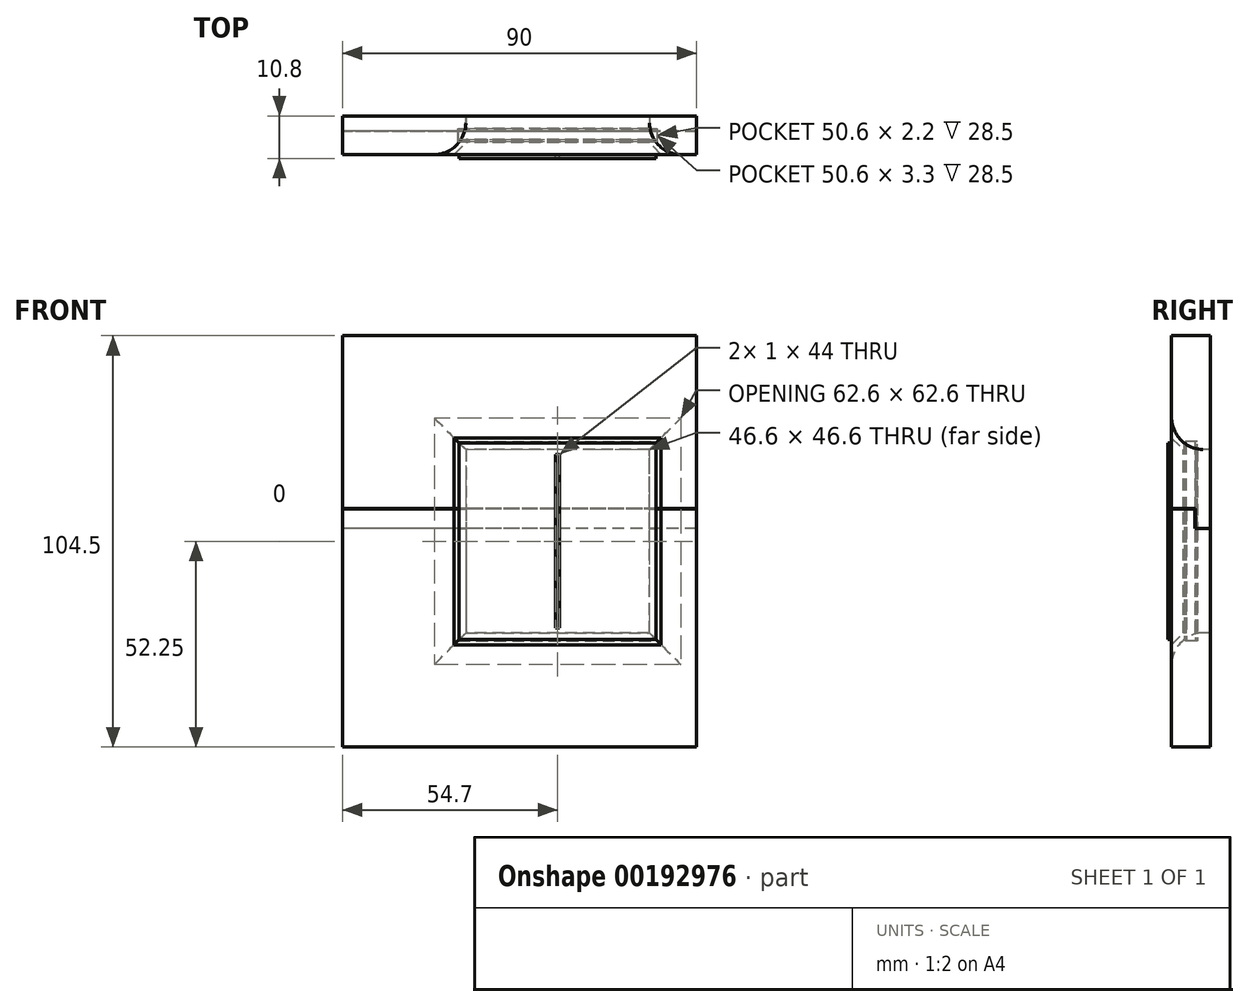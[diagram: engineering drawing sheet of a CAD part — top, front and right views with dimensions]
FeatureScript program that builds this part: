
annotation { "Feature Type Name" : "Feature", "Feature Type Description" : "" }
export const myFeature = defineFeature(function(context is Context, id is Id, definition is map)
    precondition{}
    {
        {
            var Q0;
            Q0=qCreatedBy(makeId("Front.planeOp"),FACE);
            var sketch = newSketch(context, id + "F0", { "sketchPlane" : qUnion([Q0])});
            skLineSegment(sketch, "E0", {"start": v(45, 5) * mm, "end": v(45, 109.5) * mm});
            skLineSegment(sketch, "E1", {"start": v(45, 109.5) * mm, "end": v(-45, 109.5) * mm});
            skLineSegment(sketch, "E2", {"start": v(-45, 109.5) * mm, "end": v(-45, 5) * mm});
            skLineSegment(sketch, "E3", {"start": v(45, 5) * mm, "end": v(-45, 5) * mm});
            skLineSegment(sketch, "E4", {"start": v(-15.6, 31.95) * mm, "end": v(35, 31.95) * mm});
            skLineSegment(sketch, "E5", {"start": v(35, 31.95) * mm, "end": v(35, 82.55) * mm});
            skLineSegment(sketch, "E6", {"start": v(-15.6, 82.55) * mm, "end": v(-15.6, 31.95) * mm});
            skLineSegment(sketch, "E7", {"start": v(-13.6, 80.55) * mm, "end": v(-13.6, 33.95) * mm});
            skLineSegment(sketch, "E8", {"start": v(33, 33.95) * mm, "end": v(33, 80.55) * mm});
            skLineSegment(sketch, "E9", {"start": v(45, 80.55) * mm, "end": v(-45, 80.55) * mm});
            skLineSegment(sketch, "E10", {"start": v(0, 0) * mm, "end": v(0, 125.52) * mm, "construction": true});
            skPoint(sketch, "E11", {"position": v(45, 57.25) * mm});
            skLineSegment(sketch, "E12", {"start": v(78.43, 57.25) * mm, "end": v(-79.16, 57.25) * mm, "construction": true});
            skPoint(sketch, "E13.orphan", {"position": v(-45, 57.25) * mm});
            skPoint(sketch, "E14", {"position": v(-15.6, 80.55) * mm});
            skPoint(sketch, "E15", {"position": v(35, 80.55) * mm});
            skPoint(sketch, "E16", {"position": v(0, 109.5) * mm});
            skPoint(sketch, "E17", {"position": v(0, 5) * mm});
            skPoint(sketch, "E18", {"position": v(35, 57.25) * mm});
            skPoint(sketch, "E19", {"position": v(33, 57.25) * mm});
            skPoint(sketch, "E20", {"position": v(-13.6, 57.25) * mm});
            skPoint(sketch, "E21", {"position": v(-15.6, 57.25) * mm});
            skPoint(sketch, "E22", {"position": v(0, 57.25) * mm});
            skLineSegment(sketch, "E23", {"start": v(33, 33.95) * mm, "end": v(-13.6, 33.95) * mm});
            skLineSegment(sketch, "E24", {"start": v(9.7, 159.6) * mm, "end": v(9.7, -24.97) * mm, "construction": true});
            skPoint(sketch, "E25", {"position": v(9.7, 5) * mm});
            skPoint(sketch, "E26", {"position": v(9.7, 31.95) * mm});
            skPoint(sketch, "E27", {"position": v(9.7, 33.95) * mm});
            skPoint(sketch, "E28", {"position": v(-45, 82.55) * mm});
            skLineSegment(sketch, "E29", {"start": v(-45, 82.55) * mm, "end": v(45, 82.55) * mm});
            skSolve(sketch);
        }
        {
            var Q0;
            Q0=qCreatedBy(makeId("Top.planeOp"),FACE);
            var sketch = newSketch(context, id + "F1", { "sketchPlane" : qUnion([Q0])});
            skLineSegment(sketch, "E30", {"start": v(-44.9, 9.8) * mm, "end": v(44.9, 9.8) * mm});
            skLineSegment(sketch, "E31", {"start": v(44.9, 9.8) * mm, "end": v(44.9, 0) * mm});
            skLineSegment(sketch, "E32", {"start": v(44.9, 0) * mm, "end": v(-44.9, 0) * mm});
            skLineSegment(sketch, "E33", {"start": v(-44.9, 0) * mm, "end": v(-44.9, 9.8) * mm});
            skLineSegment(sketch, "E34", {"start": v(-13.5, 3.23) * mm, "end": v(37, 3.22) * mm});
            skLineSegment(sketch, "E35", {"start": v(37, 3.22) * mm, "end": v(37, 6.58) * mm});
            skLineSegment(sketch, "E36", {"start": v(37, 6.58) * mm, "end": v(-13.5, 6.58) * mm});
            skLineSegment(sketch, "E37", {"start": v(-13.5, 6.58) * mm, "end": v(-13.5, 3.23) * mm});
            skPoint(sketch, "E38", {"position": v(0, 3.3) * mm});
            skLineSegment(sketch, "E39", {"start": v(0, -4.46) * mm, "end": v(0, 13.78) * mm, "construction": true});
            skPoint(sketch, "E40.orphan", {"position": v(0, 9.8) * mm});
            skPoint(sketch, "E41", {"position": v(0, 6.5) * mm});
            skLineSegment(sketch, "E42", {"start": v(-53.04, 4.9) * mm, "end": v(50.84, 4.9) * mm, "construction": true});
            skPoint(sketch, "E43.orphan", {"position": v(-44.9, 4.9) * mm});
            skPoint(sketch, "E44.orphan", {"position": v(44.9, 4.9) * mm});
            skPoint(sketch, "E45", {"position": v(-13.5, 4.9) * mm});
            skPoint(sketch, "E46", {"position": v(37, 4.9) * mm});
            skLineSegment(sketch, "E47", {"start": v(37, 6.58) * mm, "end": v(44.9, 6.58) * mm});
            skLineSegment(sketch, "E48", {"start": v(37, 3.22) * mm, "end": v(44.9, 3.22) * mm});
            skLineSegment(sketch, "E49", {"start": v(-13.5, 6.58) * mm, "end": v(-44.9, 6.58) * mm});
            skLineSegment(sketch, "E50", {"start": v(-13.5, 3.23) * mm, "end": v(-44.9, 3.23) * mm});
            skLineSegment(sketch, "E51", {"start": v(37, 9.8) * mm, "end": v(37, 0) * mm, "construction": true});
            skSolve(sketch);
        }
        {
            var Q0;
            Q0=qCreatedBy(makeId("Top.planeOp"),FACE);
            var sketch = newSketch(context, id + "F2", { "sketchPlane" : qUnion([Q0])});
            skLineSegment(sketch, "E52", {"start": v(-44.95, 9.8) * mm, "end": v(44.95, 9.8) * mm});
            skLineSegment(sketch, "E53", {"start": v(44.95, 9.8) * mm, "end": v(44.95, 0) * mm});
            skLineSegment(sketch, "E54", {"start": v(44.95, 0) * mm, "end": v(-44.95, 0) * mm});
            skLineSegment(sketch, "E55", {"start": v(-44.95, 0) * mm, "end": v(-44.95, 9.8) * mm});
            skLineSegment(sketch, "E56", {"start": v(-14.05, 3.8) * mm, "end": v(36.95, 3.8) * mm});
            skLineSegment(sketch, "E57", {"start": v(36.95, 3.8) * mm, "end": v(36.95, 6) * mm});
            skLineSegment(sketch, "E58", {"start": v(36.95, 6) * mm, "end": v(-14.05, 6) * mm});
            skLineSegment(sketch, "E59", {"start": v(-14.05, 6) * mm, "end": v(-14.05, 3.8) * mm});
            skPoint(sketch, "E60", {"position": v(0, 3.8) * mm});
            skLineSegment(sketch, "E61", {"start": v(0, -9.74) * mm, "end": v(0, 18.36) * mm, "construction": true});
            skPoint(sketch, "E62.orphan", {"position": v(0, 9.8) * mm});
            skPoint(sketch, "E63", {"position": v(0, 6) * mm});
            skLineSegment(sketch, "E64", {"start": v(-52.89, 4.9) * mm, "end": v(51, 4.9) * mm, "construction": true});
            skPoint(sketch, "E65.orphan", {"position": v(-44.95, 4.9) * mm});
            skPoint(sketch, "E66.orphan", {"position": v(44.95, 4.9) * mm});
            skPoint(sketch, "E67", {"position": v(-14.05, 4.9) * mm});
            skPoint(sketch, "E68", {"position": v(36.95, 4.9) * mm});
            skPoint(sketch, "E69", {"position": v(-45, 5) * mm});
            skSolve(sketch);
        }
        {
            var Q0;
            Q0=qCreatedBy(makeId("Right.planeOp"),FACE);
            var sketch = newSketch(context, id + "F3", { "sketchPlane" : qUnion([Q0])});
            skPoint(sketch, "E70.0", {"position": v(0, 0) * mm});
            skPoint(sketch, "E71.0", {"position": v(9.8, 0) * mm});
            skLineSegment(sketch, "E72", {"start": v(0, 0) * mm, "end": v(0, 109.5) * mm});
            skPoint(sketch, "E73.0", {"position": v(0, 109.5) * mm});
            skLineSegment(sketch, "E74", {"start": v(9.8, 0) * mm, "end": v(9.8, 109.5) * mm});
            skLineSegment(sketch, "E75", {"start": v(9.8, 109.5) * mm, "end": v(0, 109.5) * mm});
            skPoint(sketch, "E76.0", {"position": v(0, 65.55) * mm});
            skPoint(sketch, "E77.0", {"position": v(3.8, 0) * mm});
            skPoint(sketch, "E77.1", {"position": v(6, 0) * mm});
            skPoint(sketch, "E77.2", {"position": v(4.9, 0) * mm});
            skLineSegment(sketch, "E78", {"start": v(3.8, 0) * mm, "end": v(3.8, 109.5) * mm, "construction": true});
            skLineSegment(sketch, "E79", {"start": v(6, 0) * mm, "end": v(6, 109.5) * mm, "construction": true});
            skLineSegment(sketch, "E80", {"start": v(0, 65.55) * mm, "end": v(6, 65.55) * mm});
            skLineSegment(sketch, "E81", {"start": v(6, 65.55) * mm, "end": v(6, 60.55) * mm});
            skLineSegment(sketch, "E82", {"start": v(6, 60.55) * mm, "end": v(9.8, 60.55) * mm});
            skLineSegment(sketch, "E83.0", {"start": v(5.9, 60.45) * mm, "end": v(9.8, 60.45) * mm});
            skLineSegment(sketch, "E83.1", {"start": v(5.9, 65.45) * mm, "end": v(5.9, 60.45) * mm});
            skLineSegment(sketch, "E83.2", {"start": v(0, 65.45) * mm, "end": v(5.9, 65.45) * mm});
            skPoint(sketch, "E84.0", {"position": v(0, 5) * mm});
            skLineSegment(sketch, "E85", {"start": v(0, 5) * mm, "end": v(9.8, 5) * mm});
            skSolve(sketch);
        }
        {
            var Q0;
            {var subQ1=sQuery(id+"F0.wireOp",EDGE,"E4");Q0=makeQuery(id+"F0.imprint","IMPRINT",FACE,{"disambiguationData":[TD([[makeQuery(id+"F0.imprint","IMPRINT",EDGE,{"derivedFrom":subQ1}),1.0]])]});}
            var Q1;
            {var subQ0=sQuery(id+"F0.wireOp",EDGE,"E7");Q1=makeQuery(id+"F0.imprint","IMPRINT",FACE,{"disambiguationData":[TD([[makeQuery(id+"F0.imprint","IMPRINT",EDGE,{"derivedFrom":subQ0}),1.0]])]});}
            var Q2;
            {var subQ3=sQuery(id+"F0.wireOp",EDGE,"E5");var subQ5=sQuery(id+"F0.wireOp",EDGE,"E29");var subQ9=makeQuery(id+"F0.imprint","INTERSECT",VERTEX,{"derivedFrom":[subQ3,subQ5]});Q2=makeQuery(id+"F0.imprint","IMPRINT",FACE,{"disambiguationData":[TD([[makeQuery(id+"F0.imprint","IMPRINT",EDGE,{"disambiguationData":[TD([[subQ9,1.0]])],"derivedFrom":subQ3}),1.0]])]});}
            var Q3;
            Q3=sQuery(id+"F2.wireOp",VERTEX,"E59.start");
            var Q4;
            Q4=sQuery(id+"F2.wireOp",VERTEX,"E59.end");
            extrude(context, id + "F4", {"entities" : qUnion([Q0, Q1, Q2]), "endBound" : BoundingType.UP_TO_VERTEX, "oppositeDirection" : true, "endBoundEntityVertex" : qUnion([Q3]), "depth" : 25 * mm, "hasSecondDirection" : true, "secondDirectionBound" : BoundingType.UP_TO_VERTEX, "secondDirectionOppositeDirection" : true, "secondDirectionBoundEntityVertex" : qUnion([Q4]), "secondDirectionDepth" : 25 * mm});
        }
        {
            var Q0;
            Q0=makeQuery(id+"F0.imprint","IMPRINT",FACE,{"disambiguationData":[TD([[makeQuery(id+"F0.imprint","IMPRINT",EDGE,{"derivedFrom":sQuery(id+"F0.wireOp",EDGE,"0nGskvCt-pikJ-7yCb-w7tX-083ZzinWyTUa")}),-1.0]])]});
            var Q1;
            {var subQ5=sQuery(id+"F0.wireOp",EDGE,"0nGskvCt-pikJ-7yCb-w7tX-083ZzinWyTUa");Q1=makeQuery(id+"F0.imprint","IMPRINT",FACE,{"disambiguationData":[TD([[makeQuery(id+"F0.imprint","IMPRINT",EDGE,{"derivedFrom":subQ5}),1.0]])]});}
            var Q2;
            {var subQ3=sQuery(id+"F0.wireOp",EDGE,"gspOLp0z-dr1c-uzJE-kCBY-WIktW6QC6pkq");Q2=makeQuery(id+"F0.imprint","IMPRINT",FACE,{"disambiguationData":[TD([[makeQuery(id+"F0.imprint","IMPRINT",EDGE,{"derivedFrom":subQ3}),1.0]])]});}
            var Q3;
            {var subQ2=sQuery(id+"F0.wireOp",EDGE,"E4");Q3=makeQuery(id+"F0.imprint","IMPRINT",FACE,{"disambiguationData":[TD([[makeQuery(id+"F0.imprint","IMPRINT",EDGE,{"derivedFrom":subQ2}),1.0]])]});}
            var Q4;
            {var subQ3=sQuery(id+"F0.wireOp",EDGE,"9AMOevDd-60uQ-wB4F-UVnO-ch0xEvAojDrQ");Q4=makeQuery(id+"F0.imprint","IMPRINT",FACE,{"disambiguationData":[TD([[makeQuery(id+"F0.imprint","IMPRINT",EDGE,{"derivedFrom":subQ3}),-1.0]])]});}
            var Q5;
            {var subQ6=sQuery(id+"F0.wireOp",EDGE,"E3");Q5=makeQuery(id+"F0.imprint","IMPRINT",FACE,{"disambiguationData":[TD([[makeQuery(id+"F0.imprint","IMPRINT",EDGE,{"derivedFrom":subQ6}),-1.0]])]});}
            var Q6;
            {var subQ0=sQuery(id+"F0.wireOp",EDGE,"E9");var subQ1=sQuery(id+"F0.wireOp",EDGE,"E0");var subQ2=makeQuery(id+"F0.imprint","INTERSECT",VERTEX,{"derivedFrom":[subQ1,subQ0]});Q6=makeQuery(id+"F0.imprint","IMPRINT",FACE,{"disambiguationData":[TD([[makeQuery(id+"F0.imprint","IMPRINT",EDGE,{"disambiguationData":[TD([[subQ2,-1.0]])],"derivedFrom":subQ1}),1.0]])]});}
            var Q7;
            {var subQ4=sQuery(id+"F0.wireOp",EDGE,"E1");Q7=makeQuery(id+"F0.imprint","IMPRINT",FACE,{"disambiguationData":[TD([[makeQuery(id+"F0.imprint","IMPRINT",EDGE,{"derivedFrom":subQ4}),1.0]])]});}
            var Q8;
            {var subQ3=sQuery(id+"F0.wireOp",EDGE,"E5");var subQ5=sQuery(id+"F0.wireOp",EDGE,"E29");var subQ9=makeQuery(id+"F0.imprint","INTERSECT",VERTEX,{"derivedFrom":[subQ3,subQ5]});Q8=makeQuery(id+"F0.imprint","IMPRINT",FACE,{"disambiguationData":[TD([[makeQuery(id+"F0.imprint","IMPRINT",EDGE,{"disambiguationData":[TD([[subQ9,1.0]])],"derivedFrom":subQ3}),1.0]])]});}
            var Q9;
            {var subQ0=sQuery(id+"F0.wireOp",EDGE,"E9");var subQ1=sQuery(id+"F0.wireOp",EDGE,"E2");var subQ2=makeQuery(id+"F0.imprint","INTERSECT",VERTEX,{"derivedFrom":[subQ1,subQ0]});Q9=makeQuery(id+"F0.imprint","IMPRINT",FACE,{"disambiguationData":[TD([[makeQuery(id+"F0.imprint","IMPRINT",EDGE,{"disambiguationData":[TD([[subQ2,1.0]])],"derivedFrom":subQ1}),1.0]])]});}
            var Q10;
            Q10=sQuery(id+"F3.wireOp",VERTEX,"E75.start");
            extrude(context, id + "F5", {"entities" : qUnion([Q0, Q1, Q2, Q3, Q4, Q5, Q6, Q7, Q8, Q9]), "endBound" : BoundingType.UP_TO_VERTEX, "oppositeDirection" : true, "endBoundEntityVertex" : qUnion([Q10]), "depth" : 25 * mm});
        }
        {
            var Q0;
            {var subQ3=sQuery(id+"F3.wireOp",EDGE,"E80");Q0=makeQuery(id+"F3.imprint","IMPRINT",FACE,{"disambiguationData":[TD([[makeQuery(id+"F3.imprint","IMPRINT",EDGE,{"derivedFrom":subQ3}),-1.0]])]});}
            var Q1;
            Q1=sQuery(id+"F0.wireOp",VERTEX,"E9.start");
            var Q2;
            Q2=sQuery(id+"F0.wireOp",VERTEX,"E9.end");
            extrude(context, id + "F6", {"entities" : qUnion([Q0]), "endBound" : BoundingType.UP_TO_VERTEX, "endBoundEntityVertex" : qUnion([Q1]), "depth" : 25 * mm, "hasSecondDirection" : true, "secondDirectionBound" : BoundingType.UP_TO_VERTEX, "secondDirectionOppositeDirection" : true, "secondDirectionBoundEntityVertex" : qUnion([Q2]), "secondDirectionDepth" : 25 * mm});
        }
        {
            var Q0;
            Q0=makeQuery(id+"F4.opExtrude","SWEPT_BODY",BODY,{"disambiguationData":[OSD([sQuery(id+"F0.wireOp",EDGE,"E4"),sQuery(id+"F0.wireOp",EDGE,"E5"),sQuery(id+"F0.wireOp",EDGE,"0nGskvCt-pikJ-7yCb-w7tX-083ZzinWyTUa"),sQuery(id+"F0.wireOp",EDGE,"E6")])]});
            var Q1;
            Q1=makeQuery(id+"F5.opExtrude","SWEPT_BODY",BODY,{"disambiguationData":[OSD([sQuery(id+"F0.wireOp",EDGE,"E0"),sQuery(id+"F0.wireOp",EDGE,"E1"),sQuery(id+"F0.wireOp",EDGE,"E2"),sQuery(id+"F0.wireOp",EDGE,"E3"),sQuery(id+"F0.wireOp",EDGE,"E7"),sQuery(id+"F0.wireOp",EDGE,"E8"),sQuery(id+"F0.wireOp",EDGE,"E9"),sQuery(id+"F0.wireOp",EDGE,"E23")])]});
            booleanBodies(context, id + "F7", {"operationType" : BooleanOperationType.SUBTRACTION, "tools" : qUnion([Q0]), "targets" : qUnion([Q1])});
        }
        {
            var Q0;
            Q0=makeQuery(id+"F5.opExtrude","TWEAK_EDGE",EDGE,{"derivedFrom":[makeQuery(id+"F0.imprint","IMPRINT",EDGE,{"derivedFrom":sQuery(id+"F0.wireOp",EDGE,"E8")}),dummyQuery(id+"F5.vertexPlane.planeOp",FACE)]});
            var Q1;
            Q1=makeQuery(id+"F5.opExtrude","TWEAK_EDGE",EDGE,{"derivedFrom":[makeQuery(id+"F0.imprint","IMPRINT",EDGE,{"derivedFrom":sQuery(id+"F0.wireOp",EDGE,"E23")}),dummyQuery(id+"F5.vertexPlane.planeOp",FACE)]});
            var Q2;
            {var subQ0=sQuery(id+"F0.wireOp",EDGE,"E9");Q2=makeQuery(id+"F5.opExtrude","TWEAK_EDGE",EDGE,{"derivedFrom":[makeQuery(id+"F0.imprint","IMPRINT",EDGE,{"disambiguationData":[TD([[makeQuery(id+"F0.imprint","INTERSECT",VERTEX,{"derivedFrom":[sQuery(id+"F0.wireOp",EDGE,"E7"),subQ0]}),1.0]])],"derivedFrom":subQ0}),dummyQuery(id+"F5.vertexPlane.planeOp",FACE)]});}
            var Q3;
            Q3=makeQuery(id+"F5.opExtrude","TWEAK_EDGE",EDGE,{"derivedFrom":[makeQuery(id+"F0.imprint","IMPRINT",EDGE,{"derivedFrom":sQuery(id+"F0.wireOp",EDGE,"E7")}),dummyQuery(id+"F5.vertexPlane.planeOp",FACE)]});
            var Q4;
            Q4=makeQuery(id+"F5.opExtrude","CAP_EDGE",EDGE,{"disambiguationData":[OSD([sQuery(id+"F0.wireOp",EDGE,"E7")])],"isStart":true});
            var Q5;
            Q5=makeQuery(id+"F5.opExtrude","CAP_EDGE",EDGE,{"disambiguationData":[OSD([sQuery(id+"F0.wireOp",EDGE,"E23")])],"isStart":true});
            var Q6;
            Q6=makeQuery(id+"F5.opExtrude","CAP_EDGE",EDGE,{"disambiguationData":[OSD([sQuery(id+"F0.wireOp",EDGE,"E8")])],"isStart":true});
            var Q7;
            Q7=makeQuery(id+"F5.opExtrude","CAP_EDGE",EDGE,{"disambiguationData":[OSD([sQuery(id+"F0.wireOp",EDGE,"E9")])],"isStart":true});
            chamfer(context, id + "F8", {"entities" : qUnion([Q0, Q1, Q2, Q3, Q4, Q5, Q6, Q7]), "width" : 3 * mm, "tangentPropagation" : true});
        }
        {
            var Q0;
            Q0=makeQuery(id+"F6.opExtrude","SWEPT_BODY",BODY,{"disambiguationData":[OSD([sQuery(id+"F3.wireOp",EDGE,"E72"),sQuery(id+"F3.wireOp",EDGE,"E74"),sQuery(id+"F3.wireOp",EDGE,"E80"),sQuery(id+"F3.wireOp",EDGE,"E81"),sQuery(id+"F3.wireOp",EDGE,"E82"),sQuery(id+"F3.wireOp",EDGE,"E83.0"),sQuery(id+"F3.wireOp",EDGE,"E83.1"),sQuery(id+"F3.wireOp",EDGE,"E83.2")])]});
            var Q1;
            Q1=makeQuery(id+"F5.opExtrude","SWEPT_BODY",BODY,{"disambiguationData":[OSD([sQuery(id+"F0.wireOp",EDGE,"E0"),sQuery(id+"F0.wireOp",EDGE,"E1"),sQuery(id+"F0.wireOp",EDGE,"E2"),sQuery(id+"F0.wireOp",EDGE,"E3"),sQuery(id+"F0.wireOp",EDGE,"E7"),sQuery(id+"F0.wireOp",EDGE,"E8"),sQuery(id+"F0.wireOp",EDGE,"E9"),sQuery(id+"F0.wireOp",EDGE,"E23")])]});
            booleanBodies(context, id + "F9", {"operationType" : BooleanOperationType.SUBTRACTION, "tools" : qUnion([Q0]), "targets" : qUnion([Q1]), "keepTools" : true});
        }
        {
            var Q0;
            {var subQ2=sQuery(id+"F0.wireOp",EDGE,"E1");Q0=makeQuery(id+"F0.imprint","IMPRINT",FACE,{"disambiguationData":[TD([[makeQuery(id+"F0.imprint","IMPRINT",EDGE,{"derivedFrom":subQ2}),1.0]])]});}
            var Q1;
            Q1=makeQuery(id+"F0.imprint","IMPRINT",FACE,{"disambiguationData":[TD([[makeQuery(id+"F0.imprint","IMPRINT",EDGE,{"derivedFrom":sQuery(id+"F0.wireOp",EDGE,"0nGskvCt-pikJ-7yCb-w7tX-083ZzinWyTUa")}),-1.0]])]});
            var Q2;
            {var subQ3=sQuery(id+"F0.wireOp",EDGE,"9AMOevDd-60uQ-wB4F-UVnO-ch0xEvAojDrQ");Q2=makeQuery(id+"F0.imprint","IMPRINT",FACE,{"disambiguationData":[TD([[makeQuery(id+"F0.imprint","IMPRINT",EDGE,{"derivedFrom":subQ3}),-1.0]])]});}
            var Q3;
            {var subQ5=sQuery(id+"F0.wireOp",EDGE,"0nGskvCt-pikJ-7yCb-w7tX-083ZzinWyTUa");Q3=makeQuery(id+"F0.imprint","IMPRINT",FACE,{"disambiguationData":[TD([[makeQuery(id+"F0.imprint","IMPRINT",EDGE,{"derivedFrom":subQ5}),1.0]])]});}
            var Q4;
            {var subQ2=sQuery(id+"F0.wireOp",EDGE,"E4");Q4=makeQuery(id+"F0.imprint","IMPRINT",FACE,{"disambiguationData":[TD([[makeQuery(id+"F0.imprint","IMPRINT",EDGE,{"derivedFrom":subQ2}),1.0]])]});}
            var Q5;
            {var subQ1=sQuery(id+"F0.wireOp",EDGE,"E3");Q5=makeQuery(id+"F0.imprint","IMPRINT",FACE,{"disambiguationData":[TD([[makeQuery(id+"F0.imprint","IMPRINT",EDGE,{"derivedFrom":subQ1}),-1.0]])]});}
            var Q6;
            {var subQ0=sQuery(id+"F0.wireOp",EDGE,"E9");var subQ1=sQuery(id+"F0.wireOp",EDGE,"E0");var subQ2=makeQuery(id+"F0.imprint","INTERSECT",VERTEX,{"derivedFrom":[subQ1,subQ0]});Q6=makeQuery(id+"F0.imprint","IMPRINT",FACE,{"disambiguationData":[TD([[makeQuery(id+"F0.imprint","IMPRINT",EDGE,{"disambiguationData":[TD([[subQ2,-1.0]])],"derivedFrom":subQ1}),1.0]])]});}
            var Q7;
            {var subQ3=sQuery(id+"F0.wireOp",EDGE,"E5");var subQ5=sQuery(id+"F0.wireOp",EDGE,"E29");var subQ9=makeQuery(id+"F0.imprint","INTERSECT",VERTEX,{"derivedFrom":[subQ3,subQ5]});Q7=makeQuery(id+"F0.imprint","IMPRINT",FACE,{"disambiguationData":[TD([[makeQuery(id+"F0.imprint","IMPRINT",EDGE,{"disambiguationData":[TD([[subQ9,1.0]])],"derivedFrom":subQ3}),1.0]])]});}
            var Q8;
            {var subQ0=sQuery(id+"F0.wireOp",EDGE,"E9");var subQ1=sQuery(id+"F0.wireOp",EDGE,"E2");var subQ2=makeQuery(id+"F0.imprint","INTERSECT",VERTEX,{"derivedFrom":[subQ1,subQ0]});Q8=makeQuery(id+"F0.imprint","IMPRINT",FACE,{"disambiguationData":[TD([[makeQuery(id+"F0.imprint","IMPRINT",EDGE,{"disambiguationData":[TD([[subQ2,1.0]])],"derivedFrom":subQ1}),1.0]])]});}
            var Q9;
            Q9=sQuery(id+"F1.wireOp",VERTEX,"E33.end");
            extrude(context, id + "F10", {"entities" : qUnion([Q0, Q1, Q2, Q3, Q4, Q5, Q6, Q7, Q8]), "endBound" : BoundingType.UP_TO_VERTEX, "oppositeDirection" : true, "endBoundEntityVertex" : qUnion([Q9]), "depth" : 25 * mm});
        }
        {
            var Q0;
            Q0=makeQuery(id+"F10.opExtrude","CAP_EDGE",EDGE,{"disambiguationData":[OSD([sQuery(id+"F0.wireOp",EDGE,"E23")])],"isStart":true});
            var Q1;
            Q1=makeQuery(id+"F10.opExtrude","CAP_EDGE",EDGE,{"disambiguationData":[OSD([sQuery(id+"F0.wireOp",EDGE,"E8")])],"isStart":true});
            var Q2;
            Q2=makeQuery(id+"F10.opExtrude","CAP_EDGE",EDGE,{"disambiguationData":[OSD([sQuery(id+"F0.wireOp",EDGE,"E7")])],"isStart":true});
            var Q3;
            Q3=makeQuery(id+"F10.opExtrude","CAP_EDGE",EDGE,{"disambiguationData":[OSD([sQuery(id+"F0.wireOp",EDGE,"E9")])],"isStart":true});
            fillet(context, id + "F11", {"entities" : qUnion([Q0, Q1, Q2, Q3]), "radius" : 8 * mm, "tangentPropagation" : true, "rho" : .4, "crossSection" : FilletCrossSection.CONIC, "allowEdgeOverflow" : false});
        }
        {
            var Q0;
            Q0=qCreatedBy(makeId("Top.planeOp"),FACE);
            var sketch = newSketch(context, id + "F12", { "sketchPlane" : qUnion([Q0])});
            skLineSegment(sketch, "E86.0", {"start": v(-44.95, 0) * mm, "end": v(-44.95, 9.8) * mm});
            skLineSegment(sketch, "E86.1", {"start": v(44.95, 0) * mm, "end": v(-44.95, 0) * mm});
            skLineSegment(sketch, "E86.2", {"start": v(-44.95, 9.8) * mm, "end": v(44.95, 9.8) * mm});
            skLineSegment(sketch, "E86.3", {"start": v(44.95, 9.8) * mm, "end": v(44.95, 0) * mm});
            skLineSegment(sketch, "E87.0", {"start": v(-52.89, 4.9) * mm, "end": v(51, 4.9) * mm, "construction": true});
            skLineSegment(sketch, "E88", {"start": v(-25.5, 3.25) * mm, "end": v(-25.5, 6.55) * mm});
            skLineSegment(sketch, "E89", {"start": v(-25.5, 6.55) * mm, "end": v(25.5, 6.55) * mm});
            skLineSegment(sketch, "E90", {"start": v(25.5, 6.55) * mm, "end": v(25.5, 3.25) * mm});
            skLineSegment(sketch, "E91", {"start": v(25.5, 3.25) * mm, "end": v(-25.5, 3.25) * mm});
            skPoint(sketch, "E92", {"position": v(-25.5, 4.9) * mm});
            skLineSegment(sketch, "E93.0", {"start": v(0, -9.74) * mm, "end": v(0, 18.36) * mm, "construction": true});
            skPoint(sketch, "E94", {"position": v(0, 6.55) * mm});
            skSolve(sketch);
        }
        {
            var Q0;
            {var subQ5=sQuery(id+"F0.wireOp",EDGE,"0nGskvCt-pikJ-7yCb-w7tX-083ZzinWyTUa");Q0=makeQuery(id+"F0.imprint","IMPRINT",FACE,{"disambiguationData":[TD([[makeQuery(id+"F0.imprint","IMPRINT",EDGE,{"derivedFrom":subQ5}),1.0]])]});}
            var Q1;
            {var subQ2=sQuery(id+"F0.wireOp",EDGE,"E4");Q1=makeQuery(id+"F0.imprint","IMPRINT",FACE,{"disambiguationData":[TD([[makeQuery(id+"F0.imprint","IMPRINT",EDGE,{"derivedFrom":subQ2}),1.0]])]});}
            var Q2;
            {var subQ0=sQuery(id+"F0.wireOp",EDGE,"E7");Q2=makeQuery(id+"F0.imprint","IMPRINT",FACE,{"disambiguationData":[TD([[makeQuery(id+"F0.imprint","IMPRINT",EDGE,{"derivedFrom":subQ0}),1.0]])]});}
            var Q3;
            {var subQ3=sQuery(id+"F0.wireOp",EDGE,"E5");var subQ5=sQuery(id+"F0.wireOp",EDGE,"E29");var subQ9=makeQuery(id+"F0.imprint","INTERSECT",VERTEX,{"derivedFrom":[subQ3,subQ5]});Q3=makeQuery(id+"F0.imprint","IMPRINT",FACE,{"disambiguationData":[TD([[makeQuery(id+"F0.imprint","IMPRINT",EDGE,{"disambiguationData":[TD([[subQ9,1.0]])],"derivedFrom":subQ3}),1.0]])]});}
            var Q4;
            Q4=sQuery(id+"F12.wireOp",VERTEX,"E90.start");
            var Q5;
            Q5=sQuery(id+"F12.wireOp",VERTEX,"E90.end");
            extrude(context, id + "F13", {"entities" : qUnion([Q0, Q1, Q2, Q3]), "endBound" : BoundingType.UP_TO_VERTEX, "oppositeDirection" : true, "endBoundEntityVertex" : qUnion([Q4]), "depth" : 25 * mm, "hasSecondDirection" : true, "secondDirectionBound" : BoundingType.UP_TO_VERTEX, "secondDirectionOppositeDirection" : true, "secondDirectionBoundEntityVertex" : qUnion([Q5]), "secondDirectionDepth" : 25 * mm});
        }
        {
            var Q0;
            {var subQ2=sQuery(id+"F0.wireOp",EDGE,"E1");Q0=makeQuery(id+"F0.imprint","IMPRINT",FACE,{"disambiguationData":[TD([[makeQuery(id+"F0.imprint","IMPRINT",EDGE,{"derivedFrom":subQ2}),1.0]])]});}
            var Q1;
            Q1=makeQuery(id+"F0.imprint","IMPRINT",FACE,{"disambiguationData":[TD([[makeQuery(id+"F0.imprint","IMPRINT",EDGE,{"derivedFrom":sQuery(id+"F0.wireOp",EDGE,"0nGskvCt-pikJ-7yCb-w7tX-083ZzinWyTUa")}),-1.0]])]});
            var Q2;
            {var subQ3=sQuery(id+"F0.wireOp",EDGE,"9AMOevDd-60uQ-wB4F-UVnO-ch0xEvAojDrQ");Q2=makeQuery(id+"F0.imprint","IMPRINT",FACE,{"disambiguationData":[TD([[makeQuery(id+"F0.imprint","IMPRINT",EDGE,{"derivedFrom":subQ3}),-1.0]])]});}
            var Q3;
            {var subQ1=sQuery(id+"F0.wireOp",EDGE,"E3");Q3=makeQuery(id+"F0.imprint","IMPRINT",FACE,{"disambiguationData":[TD([[makeQuery(id+"F0.imprint","IMPRINT",EDGE,{"derivedFrom":subQ1}),-1.0]])]});}
            var Q4;
            {var subQ3=sQuery(id+"F0.wireOp",EDGE,"gspOLp0z-dr1c-uzJE-kCBY-WIktW6QC6pkq");Q4=makeQuery(id+"F0.imprint","IMPRINT",FACE,{"disambiguationData":[TD([[makeQuery(id+"F0.imprint","IMPRINT",EDGE,{"derivedFrom":subQ3}),1.0]])]});}
            var Q5;
            {var subQ5=sQuery(id+"F0.wireOp",EDGE,"0nGskvCt-pikJ-7yCb-w7tX-083ZzinWyTUa");Q5=makeQuery(id+"F0.imprint","IMPRINT",FACE,{"disambiguationData":[TD([[makeQuery(id+"F0.imprint","IMPRINT",EDGE,{"derivedFrom":subQ5}),1.0]])]});}
            var Q6;
            {var subQ2=sQuery(id+"F0.wireOp",EDGE,"E4");Q6=makeQuery(id+"F0.imprint","IMPRINT",FACE,{"disambiguationData":[TD([[makeQuery(id+"F0.imprint","IMPRINT",EDGE,{"derivedFrom":subQ2}),1.0]])]});}
            var Q7;
            {var subQ0=sQuery(id+"F0.wireOp",EDGE,"E9");var subQ1=sQuery(id+"F0.wireOp",EDGE,"E0");var subQ2=makeQuery(id+"F0.imprint","INTERSECT",VERTEX,{"derivedFrom":[subQ1,subQ0]});Q7=makeQuery(id+"F0.imprint","IMPRINT",FACE,{"disambiguationData":[TD([[makeQuery(id+"F0.imprint","IMPRINT",EDGE,{"disambiguationData":[TD([[subQ2,-1.0]])],"derivedFrom":subQ1}),1.0]])]});}
            var Q8;
            {var subQ3=sQuery(id+"F0.wireOp",EDGE,"E5");var subQ5=sQuery(id+"F0.wireOp",EDGE,"E29");var subQ9=makeQuery(id+"F0.imprint","INTERSECT",VERTEX,{"derivedFrom":[subQ3,subQ5]});Q8=makeQuery(id+"F0.imprint","IMPRINT",FACE,{"disambiguationData":[TD([[makeQuery(id+"F0.imprint","IMPRINT",EDGE,{"disambiguationData":[TD([[subQ9,1.0]])],"derivedFrom":subQ3}),1.0]])]});}
            var Q9;
            {var subQ0=sQuery(id+"F0.wireOp",EDGE,"E9");var subQ1=sQuery(id+"F0.wireOp",EDGE,"E2");var subQ2=makeQuery(id+"F0.imprint","INTERSECT",VERTEX,{"derivedFrom":[subQ1,subQ0]});Q9=makeQuery(id+"F0.imprint","IMPRINT",FACE,{"disambiguationData":[TD([[makeQuery(id+"F0.imprint","IMPRINT",EDGE,{"disambiguationData":[TD([[subQ2,1.0]])],"derivedFrom":subQ1}),1.0]])]});}
            var Q10;
            Q10=sQuery(id+"F3.wireOp",VERTEX,"E71.0");
            extrude(context, id + "F14", {"entities" : qUnion([Q0, Q1, Q2, Q3, Q4, Q5, Q6, Q7, Q8, Q9]), "endBound" : BoundingType.UP_TO_VERTEX, "oppositeDirection" : true, "endBoundEntityVertex" : qUnion([Q10]), "depth" : 25 * mm});
        }
        {
            var Q0;
            {var subQ3=sQuery(id+"F3.wireOp",EDGE,"E80");Q0=makeQuery(id+"F3.imprint","IMPRINT",FACE,{"disambiguationData":[TD([[makeQuery(id+"F3.imprint","IMPRINT",EDGE,{"derivedFrom":subQ3}),-1.0]])]});}
            var Q1;
            Q1=sQuery(id+"F0.wireOp",VERTEX,"E9.start");
            var Q2;
            Q2=sQuery(id+"F0.wireOp",VERTEX,"E9.end");
            extrude(context, id + "F15", {"entities" : qUnion([Q0]), "endBound" : BoundingType.UP_TO_VERTEX, "endBoundEntityVertex" : qUnion([Q1]), "depth" : 25 * mm, "hasSecondDirection" : true, "secondDirectionBound" : BoundingType.UP_TO_VERTEX, "secondDirectionOppositeDirection" : true, "secondDirectionBoundEntityVertex" : qUnion([Q2]), "secondDirectionDepth" : 25 * mm});
        }
        {
            var Q0;
            Q0=makeQuery(id+"F13.opExtrude","SWEPT_BODY",BODY,{"disambiguationData":[OSD([sQuery(id+"F0.wireOp",EDGE,"E4"),sQuery(id+"F0.wireOp",EDGE,"E5"),sQuery(id+"F0.wireOp",EDGE,"0nGskvCt-pikJ-7yCb-w7tX-083ZzinWyTUa"),sQuery(id+"F0.wireOp",EDGE,"E6")])]});
            var Q1;
            Q1=makeQuery(id+"F14.opExtrude","SWEPT_BODY",BODY,{"disambiguationData":[OSD([sQuery(id+"F0.wireOp",EDGE,"E0"),sQuery(id+"F0.wireOp",EDGE,"E1"),sQuery(id+"F0.wireOp",EDGE,"E2"),sQuery(id+"F0.wireOp",EDGE,"E3"),sQuery(id+"F0.wireOp",EDGE,"E7"),sQuery(id+"F0.wireOp",EDGE,"E8"),sQuery(id+"F0.wireOp",EDGE,"E9"),sQuery(id+"F0.wireOp",EDGE,"E23")])]});
            booleanBodies(context, id + "F16", {"operationType" : BooleanOperationType.SUBTRACTION, "tools" : qUnion([Q0]), "targets" : qUnion([Q1])});
        }
        {
            var Q0;
            Q0=makeQuery(id+"F14.opExtrude","TWEAK_EDGE",EDGE,{"derivedFrom":[makeQuery(id+"F0.imprint","IMPRINT",EDGE,{"derivedFrom":sQuery(id+"F0.wireOp",EDGE,"E8")}),dummyQuery(id+"F14.vertexPlane.planeOp",FACE)]});
            var Q1;
            Q1=makeQuery(id+"F14.opExtrude","TWEAK_EDGE",EDGE,{"derivedFrom":[makeQuery(id+"F0.imprint","IMPRINT",EDGE,{"derivedFrom":sQuery(id+"F0.wireOp",EDGE,"E23")}),dummyQuery(id+"F14.vertexPlane.planeOp",FACE)]});
            var Q2;
            {var subQ0=sQuery(id+"F0.wireOp",EDGE,"E9");Q2=makeQuery(id+"F14.opExtrude","TWEAK_EDGE",EDGE,{"derivedFrom":[makeQuery(id+"F0.imprint","IMPRINT",EDGE,{"disambiguationData":[TD([[makeQuery(id+"F0.imprint","INTERSECT",VERTEX,{"derivedFrom":[sQuery(id+"F0.wireOp",EDGE,"E7"),subQ0]}),1.0]])],"derivedFrom":subQ0}),dummyQuery(id+"F14.vertexPlane.planeOp",FACE)]});}
            var Q3;
            Q3=makeQuery(id+"F14.opExtrude","TWEAK_EDGE",EDGE,{"derivedFrom":[makeQuery(id+"F0.imprint","IMPRINT",EDGE,{"derivedFrom":sQuery(id+"F0.wireOp",EDGE,"E7")}),dummyQuery(id+"F14.vertexPlane.planeOp",FACE)]});
            var Q4;
            Q4=makeQuery(id+"F14.opExtrude","CAP_EDGE",EDGE,{"disambiguationData":[OSD([sQuery(id+"F0.wireOp",EDGE,"E23")])],"isStart":true});
            var Q5;
            Q5=makeQuery(id+"F14.opExtrude","CAP_EDGE",EDGE,{"disambiguationData":[OSD([sQuery(id+"F0.wireOp",EDGE,"E7")])],"isStart":true});
            var Q6;
            Q6=makeQuery(id+"F14.opExtrude","CAP_EDGE",EDGE,{"disambiguationData":[OSD([sQuery(id+"F0.wireOp",EDGE,"E9")])],"isStart":true});
            var Q7;
            Q7=makeQuery(id+"F14.opExtrude","CAP_EDGE",EDGE,{"disambiguationData":[OSD([sQuery(id+"F0.wireOp",EDGE,"E8")])],"isStart":true});
            chamfer(context, id + "F17", {"entities" : qUnion([Q0, Q1, Q2, Q3, Q4, Q5, Q6, Q7]), "width" : 3 * mm, "tangentPropagation" : true});
        }
        {
            var Q0;
            Q0=makeQuery(id+"F15.opExtrude","SWEPT_BODY",BODY,{"disambiguationData":[OSD([sQuery(id+"F3.wireOp",EDGE,"E72"),sQuery(id+"F3.wireOp",EDGE,"E74"),sQuery(id+"F3.wireOp",EDGE,"E80"),sQuery(id+"F3.wireOp",EDGE,"E81"),sQuery(id+"F3.wireOp",EDGE,"E82"),sQuery(id+"F3.wireOp",EDGE,"E83.0"),sQuery(id+"F3.wireOp",EDGE,"E83.1"),sQuery(id+"F3.wireOp",EDGE,"E83.2")])]});
            var Q1;
            Q1=makeQuery(id+"F14.opExtrude","SWEPT_BODY",BODY,{"disambiguationData":[OSD([sQuery(id+"F0.wireOp",EDGE,"E0"),sQuery(id+"F0.wireOp",EDGE,"E1"),sQuery(id+"F0.wireOp",EDGE,"E2"),sQuery(id+"F0.wireOp",EDGE,"E3"),sQuery(id+"F0.wireOp",EDGE,"E7"),sQuery(id+"F0.wireOp",EDGE,"E8"),sQuery(id+"F0.wireOp",EDGE,"E9"),sQuery(id+"F0.wireOp",EDGE,"E23")])]});
            booleanBodies(context, id + "F18", {"operationType" : BooleanOperationType.SUBTRACTION, "tools" : qUnion([Q0]), "targets" : qUnion([Q1]), "keepTools" : true});
        }
        {
            var Q0;
            {var subQ4=sQuery(id+"F0.wireOp",EDGE,"E1");Q0=makeQuery(id+"F0.imprint","IMPRINT",FACE,{"disambiguationData":[TD([[makeQuery(id+"F0.imprint","IMPRINT",EDGE,{"derivedFrom":subQ4}),1.0]])]});}
            var sketch = newSketch(context, id + "F19", { "sketchPlane" : qUnion([Q0])});
            skLineSegment(sketch, "E95.0", {"start": v(78.43, 57.25) * mm, "end": v(-79.16, 57.25) * mm, "construction": true});
            skLineSegment(sketch, "E96.0", {"start": v(9.7, 159.6) * mm, "end": v(9.7, -24.97) * mm, "construction": true});
            skPoint(sketch, "E97", {"position": v(9.7, 57.25) * mm});
            skLineSegment(sketch, "E98.bottom", {"start": v(34.7, 82.25) * mm, "end": v(-15.3, 82.25) * mm});
            skLineSegment(sketch, "E98.top", {"start": v(34.7, 32.25) * mm, "end": v(-15.3, 32.25) * mm});
            skLineSegment(sketch, "E98.left", {"start": v(34.7, 82.25) * mm, "end": v(34.7, 32.25) * mm});
            skLineSegment(sketch, "E98.right", {"start": v(-15.3, 82.25) * mm, "end": v(-15.3, 32.25) * mm});
            skLineSegment(sketch, "E99.bottom", {"start": v(10.2, 79.25) * mm, "end": v(9.2, 79.25) * mm});
            skLineSegment(sketch, "E99.top", {"start": v(10.2, 35.25) * mm, "end": v(9.2, 35.25) * mm});
            skLineSegment(sketch, "E99.left", {"start": v(10.2, 79.25) * mm, "end": v(10.2, 35.25) * mm});
            skLineSegment(sketch, "E99.right", {"start": v(9.2, 79.25) * mm, "end": v(9.2, 35.25) * mm});
            skSolve(sketch);
        }
        {
            var Q0;
            Q0=makeQuery(id+"F19.imprint","IMPRINT",FACE,{"disambiguationData":[TD([[makeQuery(id+"F19.imprint","IMPRINT",EDGE,{"derivedFrom":sQuery(id+"F19.wireOp",EDGE,"E98.bottom")}),1.0]])]});
            extrude(context, id + "F20", {"entities" : qUnion([Q0]), "depth" : 1 * mm, "offsetDistance" : 25 * mm});
        }
    });
